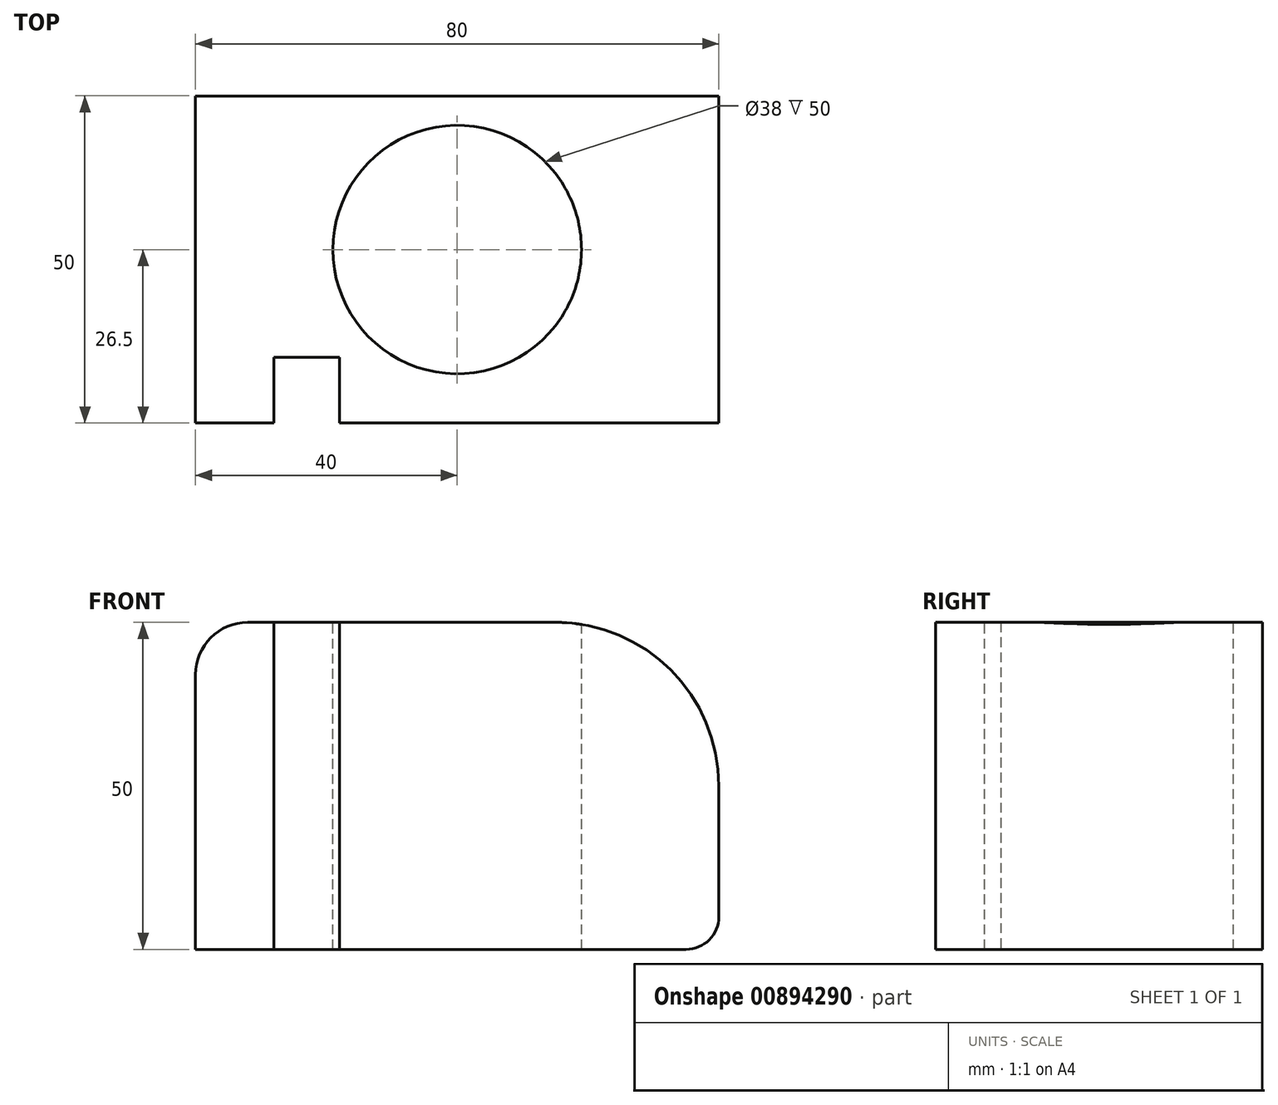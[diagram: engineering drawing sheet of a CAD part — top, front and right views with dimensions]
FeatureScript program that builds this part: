
annotation { "Feature Type Name" : "Feature", "Feature Type Description" : "" }
export const myFeature = defineFeature(function(context is Context, id is Id, definition is map)
    precondition{}
    {
        {
            var Q0;
            Q0=qCreatedBy(makeId("Top.planeOp"),FACE);
            var sketch = newSketch(context, id + "F0", { "sketchPlane" : qUnion([Q0])});
            skLineSegment(sketch, "E0.bottom", {"start": v(40, -26.5) * mm, "end": v(-40, -26.5) * mm});
            skLineSegment(sketch, "E0.top", {"start": v(40, 23.5) * mm, "end": v(-40, 23.5) * mm});
            skLineSegment(sketch, "E0.left", {"start": v(40, -26.5) * mm, "end": v(40, 23.5) * mm});
            skLineSegment(sketch, "E0.right", {"start": v(-40, -26.5) * mm, "end": v(-40, 23.5) * mm});
            skPoint(sketch, "E0.middle", {"position": v(0, -1.5) * mm});
            skCircle(sketch, "E1", {"center": v(0, 0) * mm, "radius": 19 * mm});
            skSolve(sketch);
        }
        {
            var Q0;
            Q0=makeQuery(id+"F0.imprint","IMPRINT",FACE,{"disambiguationData":[TD([[makeQuery(id+"F0.imprint","IMPRINT",EDGE,{"derivedFrom":sQuery(id+"F0.wireOp",EDGE,"E0.bottom")}),-1.0]])]});
            extrude(context, id + "F1", {"entities" : qUnion([Q0]), "oppositeDirection" : true, "depth" : 50 * mm, "offsetDistance" : 25 * mm});
        }
        {
            var Q0;
            Q0=makeQuery(id+"F1.opExtrude","CAP_EDGE",EDGE,{"disambiguationData":[OSD([sQuery(id+"F0.wireOp",EDGE,"E0.left")])],"isStart":true});
            fillet(context, id + "F2", {"entities" : qUnion([Q0]), "radius" : 25 * mm, "tangentPropagation" : true, "allowEdgeOverflow" : false});
        }
        {
            var Q0;
            Q0=makeQuery(id+"F1.opExtrude","CAP_EDGE",EDGE,{"disambiguationData":[OSD([sQuery(id+"F0.wireOp",EDGE,"E0.left")])],"isStart":false});
            fillet(context, id + "F3", {"entities" : qUnion([Q0]), "radius" : 5 * mm, "tangentPropagation" : true, "allowEdgeOverflow" : false});
        }
        {
            var Q0;
            Q0=makeQuery(id+"F1.opExtrude","CAP_EDGE",EDGE,{"disambiguationData":[OSD([sQuery(id+"F0.wireOp",EDGE,"E0.right")])],"isStart":true});
            fillet(context, id + "F4", {"entities" : qUnion([Q0]), "radius" : 8 * mm, "tangentPropagation" : true, "defaultsChanged" : true, "vertexSettings" : [], "allowEdgeOverflow" : false});
        }
        {
            var Q0;
            Q0=makeQuery(id+"F1.opExtrude","SWEPT_FACE",FACE,{"disambiguationData":[OSD([sQuery(id+"F0.wireOp",EDGE,"E0.bottom")])]});
            var sketch = newSketch(context, id + "F5", { "sketchPlane" : qUnion([Q0])});
            skLineSegment(sketch, "E2", {"start": v(-28, 0) * mm, "end": v(-28, -50) * mm});
            skLineSegment(sketch, "E3", {"start": v(-28, -50) * mm, "end": v(-18, -50) * mm});
            skLineSegment(sketch, "E4", {"start": v(-18, -50) * mm, "end": v(-18, 0) * mm});
            skLineSegment(sketch, "E5", {"start": v(-18, 0) * mm, "end": v(-28, 0) * mm});
            skSolve(sketch);
        }
        {
            var Q0;
            Q0=makeQuery(id+"F5.imprint","IMPRINT",FACE,{"disambiguationData":[TD([[makeQuery(id+"F5.imprint","IMPRINT",EDGE,{"derivedFrom":sQuery(id+"F5.wireOp",EDGE,"E2")}),1.0]])]});
            extrude(context, id + "F6", {"entities" : qUnion([Q0]), "operationType" : NewBodyOperationType.REMOVE, "oppositeDirection" : true, "depth" : 10 * mm, "offsetDistance" : 25 * mm});
        }
    });
